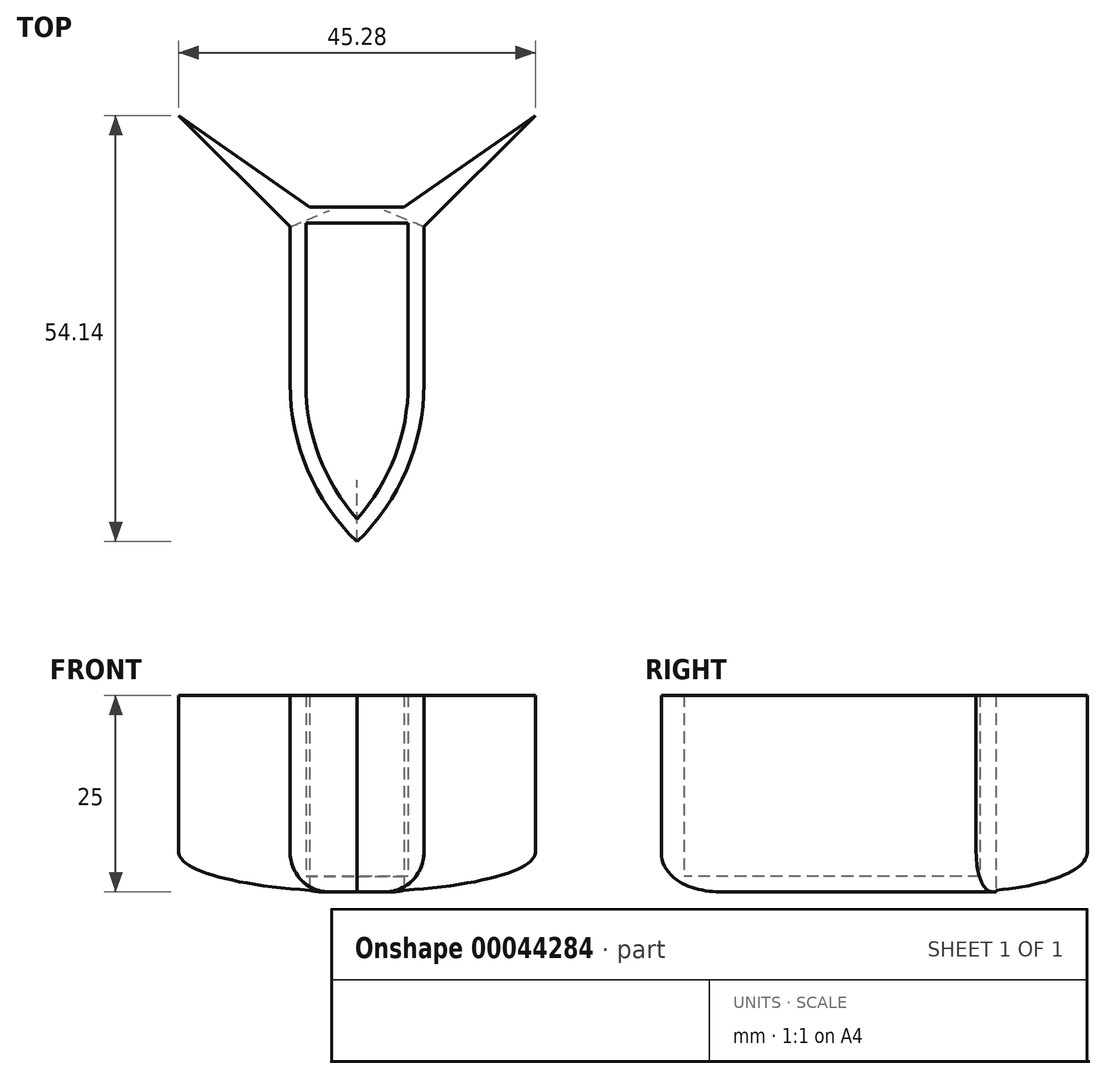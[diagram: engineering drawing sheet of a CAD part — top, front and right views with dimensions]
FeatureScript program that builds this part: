
annotation { "Feature Type Name" : "Feature", "Feature Type Description" : "" }
export const myFeature = defineFeature(function(context is Context, id is Id, definition is map)
    precondition{}
    {
        {
            var Q0;
            Q0=qCreatedBy(makeId("Top.planeOp"),FACE);
            var sketch = newSketch(context, id + "F0", { "sketchPlane" : qUnion([Q0])});
            skLineSegment(sketch, "E0", {"start": v(-22.64, 13.66) * mm, "end": v(-8.5, -0.48) * mm});
            skLineSegment(sketch, "E1", {"start": v(-8.5, -0.48) * mm, "end": v(-8.5, -20.48) * mm});
            skLineSegment(sketch, "E2", {"start": v(-22.64, 13.66) * mm, "end": v(-6, 2.01) * mm});
            skLineSegment(sketch, "E3", {"start": v(-6, 2.01) * mm, "end": v(0, 2.01) * mm});
            skArc(sketch, "E4", {"start": v(-8.5, -20.48) * mm, "mid": v(-6.29, -31.34) * mm, "end": v(0, -40.48) * mm});
            skArc(sketch, "E5.MirrorCS", {"start": v(8.5, -20.48) * mm, "mid": v(6.29, -31.34) * mm, "end": v(0, -40.48) * mm});
            skLineSegment(sketch, "E6.MirrorCS", {"start": v(22.64, 13.66) * mm, "end": v(8.5, -0.48) * mm});
            skLineSegment(sketch, "E7.MirrorCS", {"start": v(22.64, 13.66) * mm, "end": v(6, 2.01) * mm});
            skLineSegment(sketch, "E8.MirrorCS", {"start": v(8.5, -0.48) * mm, "end": v(8.5, -20.48) * mm});
            skLineSegment(sketch, "E9.MirrorCS", {"start": v(6, 2.01) * mm, "end": v(0, 2.01) * mm});
            skSolve(sketch);
        }
        {
            var Q0;
            Q0=makeQuery(id+"F0.imprint","IMPRINT",FACE,{"disambiguationData":[TD([[makeQuery(id+"F0.imprint","IMPRINT",EDGE,{"derivedFrom":sQuery(id+"F0.wireOp",EDGE,"E0")}),1.0]])]});
            extrude(context, id + "F1", {"entities" : qUnion([Q0]), "depth" : 25 * mm});
        }
        {
            var Q0;
            Q0=makeQuery(id+"F1.opExtrude","CAP_FACE",FACE,{"disambiguationData":[OSD([sQuery(id+"F0.wireOp",EDGE,"E0"),sQuery(id+"F0.wireOp",EDGE,"E1"),sQuery(id+"F0.wireOp",EDGE,"E2"),sQuery(id+"F0.wireOp",EDGE,"E3"),sQuery(id+"F0.wireOp",EDGE,"E4"),sQuery(id+"F0.wireOp",EDGE,"E5.MirrorCS"),sQuery(id+"F0.wireOp",EDGE,"E6.MirrorCS"),sQuery(id+"F0.wireOp",EDGE,"E7.MirrorCS"),sQuery(id+"F0.wireOp",EDGE,"E8.MirrorCS"),sQuery(id+"F0.wireOp",EDGE,"E9.MirrorCS")])],"isStart":false});
            shell(context, id + "F2", {"entities" : qUnion([Q0]), "thickness" : 2 * mm});
        }
        {
            var Q0;
            Q0=makeQuery(id+"F1.opExtrude","CAP_EDGE",EDGE,{"disambiguationData":[OSD([sQuery(id+"F0.wireOp",EDGE,"E5.MirrorCS")])],"isStart":true});
            var Q1;
            Q1=makeQuery(id+"F1.opExtrude","CAP_EDGE",EDGE,{"disambiguationData":[OSD([sQuery(id+"F0.wireOp",EDGE,"E4")])],"isStart":true});
            var Q2;
            Q2=makeQuery(id+"F1.opExtrude","CAP_EDGE",EDGE,{"disambiguationData":[OSD([sQuery(id+"F0.wireOp",EDGE,"E8.MirrorCS")])],"isStart":true});
            var Q3;
            Q3=makeQuery(id+"F1.opExtrude","CAP_EDGE",EDGE,{"disambiguationData":[OSD([sQuery(id+"F0.wireOp",EDGE,"E1")])],"isStart":true});
            var Q4;
            Q4=makeQuery(id+"F1.opExtrude","CAP_EDGE",EDGE,{"disambiguationData":[OSD([sQuery(id+"F0.wireOp",EDGE,"E6.MirrorCS")])],"isStart":true});
            var Q5;
            Q5=makeQuery(id+"F1.opExtrude","CAP_EDGE",EDGE,{"disambiguationData":[OSD([sQuery(id+"F0.wireOp",EDGE,"E0")])],"isStart":true});
            fillet(context, id + "F3", {"entities" : qUnion([Q0, Q1, Q2, Q3, Q4, Q5]), "radius" : 5 * mm, "tangentPropagation" : true, "allowEdgeOverflow" : false});
        }
    });
